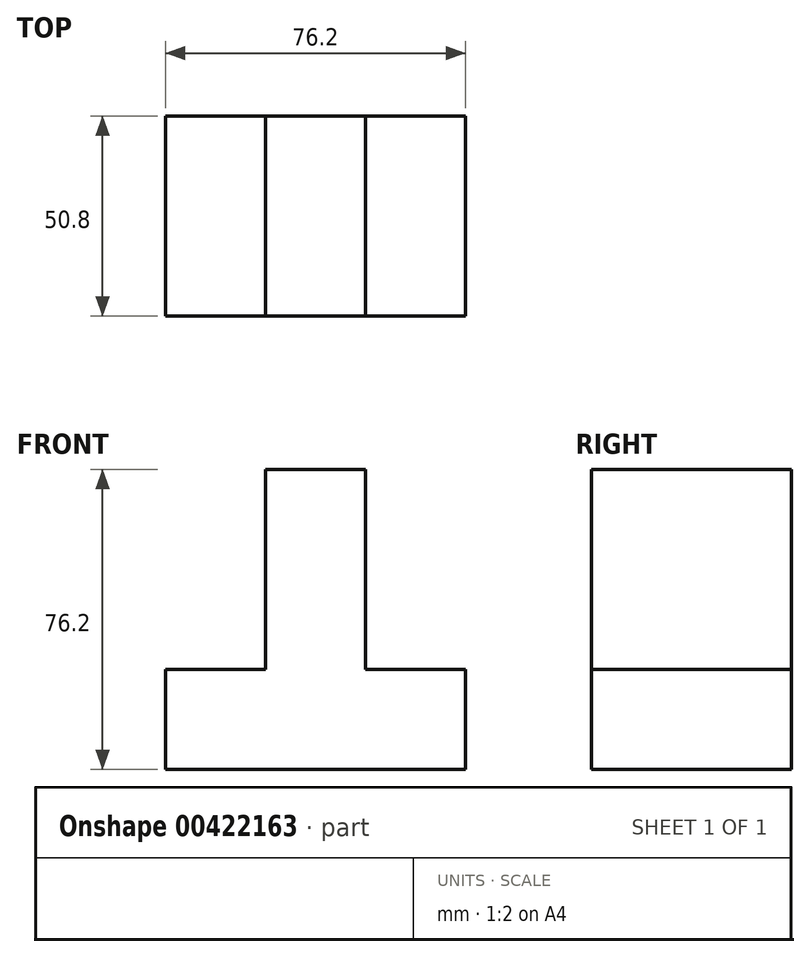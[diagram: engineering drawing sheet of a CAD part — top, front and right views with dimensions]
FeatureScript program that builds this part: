
annotation { "Feature Type Name" : "Feature", "Feature Type Description" : "" }
export const myFeature = defineFeature(function(context is Context, id is Id, definition is map)
    precondition{}
    {
        {
            var Q0;
            Q0=qCreatedBy(makeId("Front.planeOp"),FACE);
            var sketch = newSketch(context, id + "F0", { "sketchPlane" : qUnion([Q0])});
            skLineSegment(sketch, "E0", {"start": v(40.49, -19.83) * mm, "end": v(-35.71, -19.83) * mm});
            skLineSegment(sketch, "E1", {"start": v(-35.71, -19.83) * mm, "end": v(-35.71, 5.57) * mm});
            skLineSegment(sketch, "E2", {"start": v(-35.71, 5.57) * mm, "end": v(-10.31, 5.57) * mm});
            skLineSegment(sketch, "E3", {"start": v(-10.31, 5.57) * mm, "end": v(-10.31, 56.37) * mm});
            skLineSegment(sketch, "E4", {"start": v(40.49, -19.83) * mm, "end": v(40.49, 5.57) * mm});
            skLineSegment(sketch, "E5", {"start": v(40.49, 5.57) * mm, "end": v(15.09, 5.57) * mm});
            skLineSegment(sketch, "E6", {"start": v(15.09, 5.57) * mm, "end": v(15.09, 56.37) * mm});
            skLineSegment(sketch, "E7", {"start": v(15.09, 56.37) * mm, "end": v(-10.31, 56.37) * mm});
            skSolve(sketch);
        }
        {
            var Q0;
            Q0=makeQuery(id+"F0.imprint","IMPRINT",FACE,{"disambiguationData":[TD([[makeQuery(id+"F0.imprint","IMPRINT",EDGE,{"derivedFrom":sQuery(id+"F0.wireOp",EDGE,"E0")}),-1.0]])]});
            extrude(context, id + "F1", {"entities" : qUnion([Q0]), "depth" : 50.8 * mm});
        }
    });
